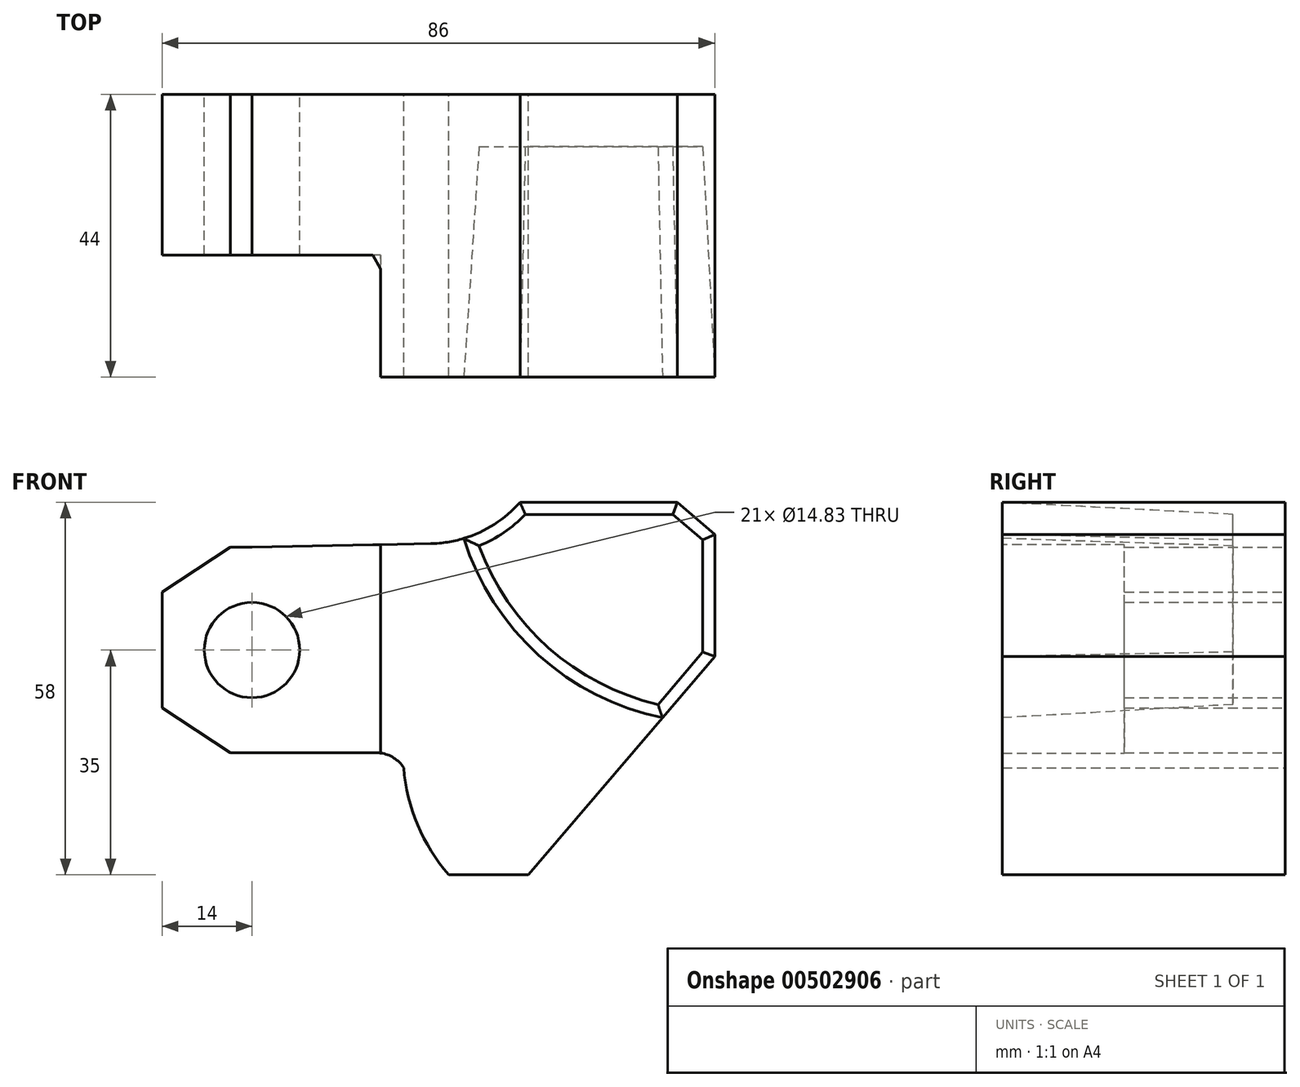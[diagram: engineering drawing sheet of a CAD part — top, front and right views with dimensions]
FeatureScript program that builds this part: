
annotation { "Feature Type Name" : "Feature", "Feature Type Description" : "" }
export const myFeature = defineFeature(function(context is Context, id is Id, definition is map)
    precondition{}
    {
        {
            var Q0;
            Q0=qCreatedBy(makeId("Front.planeOp"),FACE);
            var sketch = newSketch(context, id + "F0", { "sketchPlane" : qUnion([Q0])});
            skLineSegment(sketch, "E0", {"start": v(0, 0) * mm, "end": v(0, 18) * mm});
            skLineSegment(sketch, "E1", {"start": v(0, 18) * mm, "end": v(10.62, 25) * mm});
            skLineSegment(sketch, "E2", {"start": v(0, 0) * mm, "end": v(10.62, -7) * mm});
            skLineSegment(sketch, "E3", {"start": v(44.6, -26) * mm, "end": v(57, -26) * mm});
            skLineSegment(sketch, "E4", {"start": v(57, -26) * mm, "end": v(81.38, 2.58) * mm});
            skLineSegment(sketch, "E5", {"start": v(81.38, 2.58) * mm, "end": v(86, 8) * mm});
            skLineSegment(sketch, "E6", {"start": v(86, 8) * mm, "end": v(86, 27) * mm});
            skLineSegment(sketch, "E7", {"start": v(86, 27) * mm, "end": v(80.14, 32) * mm});
            skLineSegment(sketch, "E8", {"start": v(80.14, 32) * mm, "end": v(55.69, 32) * mm});
            skCircle(sketch, "E9", {"center": v(14, 9) * mm, "radius": 7.42 * mm});
            skPoint(sketch, "E9.centerSnap0", {"position": v(0, 9) * mm});
            skArc(sketch, "E10", {"start": v(41.82, 25.57) * mm, "mid": v(49.43, 27.33) * mm, "end": v(55.69, 32) * mm});
            skLineSegment(sketch, "E11", {"start": v(10.62, 25) * mm, "end": v(14, 25) * mm});
            skLineSegment(sketch, "E12", {"start": v(14, 25) * mm, "end": v(41.82, 25.57) * mm});
            skArc(sketch, "E13", {"start": v(37.6, -9.34) * mm, "mid": v(39.76, -18.23) * mm, "end": v(44.6, -26) * mm});
            skLineSegment(sketch, "E14", {"start": v(10.62, -7) * mm, "end": v(33.36, -7) * mm});
            skArc(sketch, "E15", {"start": v(37.6, -9.34) * mm, "mid": v(35.78, -7.62) * mm, "end": v(33.36, -7) * mm});
            skSolve(sketch);
        }
        {
            var Q0;
            Q0=makeQuery(id+"F0.imprint","IMPRINT",FACE,{"disambiguationData":[TD([[makeQuery(id+"F0.imprint","IMPRINT",EDGE,{"derivedFrom":sQuery(id+"F0.wireOp",EDGE,"E0")}),-1.0]])]});
            extrude(context, id + "F1", {"entities" : qUnion([Q0]), "depth" : 44 * mm});
        }
        {
            var Q0;
            Q0=makeQuery(id+"F1.opExtrude","SWEPT_FACE",FACE,{"disambiguationData":[OSD([sQuery(id+"F0.wireOp",EDGE,"E0")])]});
            var sketch = newSketch(context, id + "F2", { "sketchPlane" : qUnion([Q0])});
            skLineSegment(sketch, "E16", {"start": v(44, 25.6) * mm, "end": v(44, -7.56) * mm});
            skLineSegment(sketch, "E17", {"start": v(44, -7.56) * mm, "end": v(25, -7.56) * mm});
            skLineSegment(sketch, "E18", {"start": v(25, -7.56) * mm, "end": v(25, 25.38) * mm});
            skLineSegment(sketch, "E19", {"start": v(25, 25.38) * mm, "end": v(44, 25.6) * mm});
            skSolve(sketch);
        }
        {
            var Q0;
            Q0 = qSketchRegion(id + "F2", true);
            extrude(context, id + "F3", {"entities" : qUnion([Q0]), "operationType" : NewBodyOperationType.REMOVE, "oppositeDirection" : true, "depth" : 34 * mm});
        }
        {
            var Q0;
            Q0=makeQuery(id+"F1.opExtrude","CAP_FACE",FACE,{"disambiguationData":[OSD([sQuery(id+"F0.wireOp",EDGE,"E0"),sQuery(id+"F0.wireOp",EDGE,"E1"),sQuery(id+"F0.wireOp",EDGE,"E2"),sQuery(id+"F0.wireOp",EDGE,"E3"),sQuery(id+"F0.wireOp",EDGE,"E4"),sQuery(id+"F0.wireOp",EDGE,"E5"),sQuery(id+"F0.wireOp",EDGE,"E6"),sQuery(id+"F0.wireOp",EDGE,"E7"),sQuery(id+"F0.wireOp",EDGE,"E8"),sQuery(id+"F0.wireOp",EDGE,"E9"),sQuery(id+"F0.wireOp",EDGE,"E10"),sQuery(id+"F0.wireOp",EDGE,"E11"),sQuery(id+"F0.wireOp",EDGE,"E12"),sQuery(id+"F0.wireOp",EDGE,"E13"),sQuery(id+"F0.wireOp",EDGE,"E14"),sQuery(id+"F0.wireOp",EDGE,"E15")])],"isStart":false});
            var sketch = newSketch(context, id + "F4", { "sketchPlane" : qUnion([Q0])});
            skLineSegment(sketch, "E20", {"start": v(86, 33.62) * mm, "end": v(86, -2.38) * mm});
            skPoint(sketch, "E20.startSnap0", {"position": v(86, 17.5) * mm});
            skCircle(sketch, "E21", {"center": v(86.08, 38.62) * mm, "radius": 41 * mm});
            skSolve(sketch);
        }
        {
            var Q0;
            {var subQ0=makeQuery(id+"F1.opExtrude","CAP_EDGE",EDGE,{"disambiguationData":[OSD([sQuery(id+"F0.wireOp",EDGE,"E7")])],"isStart":false});Q0=makeQuery(id+"F4.imprint","IMPRINT",FACE,{"disambiguationData":[TD([[makeQuery(id+"F4.imprint","IMPRINT",EDGE,{"derivedFrom":subQ0}),1.0]])]});}
            extrude(context, id + "F5", {"entities" : qUnion([Q0]), "operationType" : NewBodyOperationType.REMOVE, "endBound" : BoundingType.SYMMETRIC, "oppositeDirection" : true, "depth" : 71.8 * mm, "hasDraft" : true, "draftAngle" : 3 * degree, "draftPullDirection" : true, "hasSecondDirection" : true, "secondDirectionOppositeDirection" : false, "secondDirectionDepth" : 12 * mm, "hasSecondDirectionDraft" : true, "secondDirectionDraftAngle" : 3 * degree});
        }
    });
